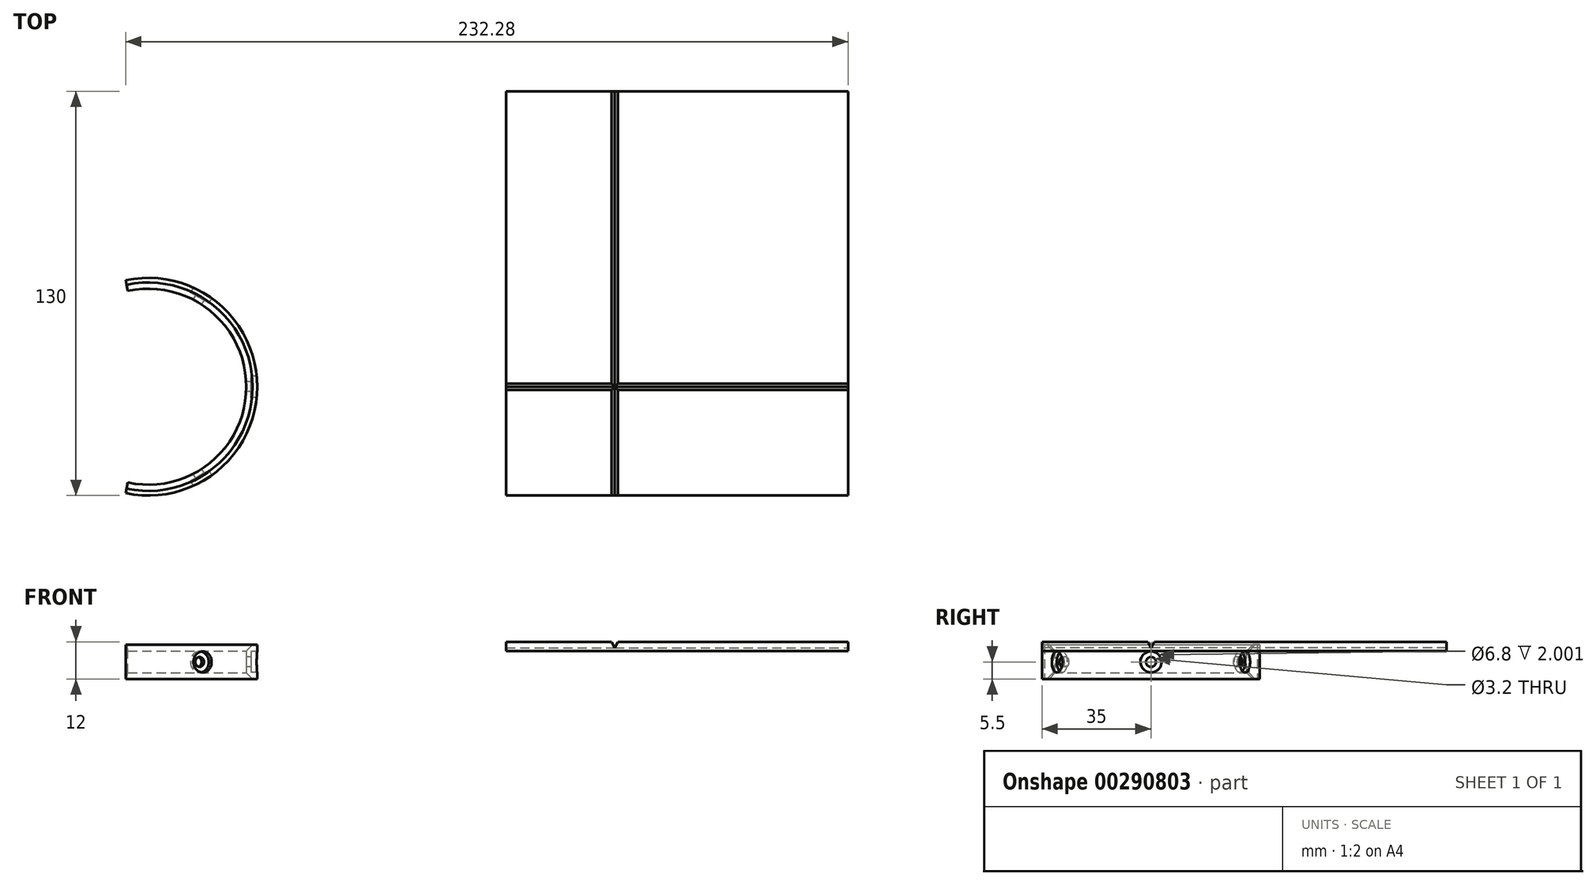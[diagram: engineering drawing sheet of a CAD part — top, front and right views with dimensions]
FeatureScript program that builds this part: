
annotation { "Feature Type Name" : "Feature", "Feature Type Description" : "" }
export const myFeature = defineFeature(function(context is Context, id is Id, definition is map)
    precondition{}
    {
        {
            var Q0;
            Q0=qCreatedBy(makeId("Top.planeOp"),FACE);
            var sketch = newSketch(context, id + "F0", { "sketchPlane" : qUnion([Q0])});
            skLineSegment(sketch, "E0.bottom", {"start": v(60, 80) * mm, "end": v(-20, 80) * mm});
            skLineSegment(sketch, "E0.top", {"start": v(60, -20) * mm, "end": v(-20, -20) * mm});
            skLineSegment(sketch, "E0.left", {"start": v(60, 80) * mm, "end": v(60, -20) * mm});
            skLineSegment(sketch, "E0.right", {"start": v(-20, 80) * mm, "end": v(-20, -20) * mm});
            skLineSegment(sketch, "E1.bottom", {"start": v(75, 95) * mm, "end": v(-35, 95) * mm});
            skLineSegment(sketch, "E1.top", {"start": v(75, -35) * mm, "end": v(-35, -35) * mm});
            skLineSegment(sketch, "E1.left", {"start": v(75, 95) * mm, "end": v(75, -35) * mm});
            skLineSegment(sketch, "E1.right", {"start": v(-35, 95) * mm, "end": v(-35, -35) * mm});
            skSolve(sketch);
        }
        {
            var Q0;
            {var subQ4=sQuery(id+"F0.wireOp",EDGE,"E0.bottom");Q0=makeQuery(id+"F0.imprint","IMPRINT",FACE,{"disambiguationData":[TD([[makeQuery(id+"F0.imprint","IMPRINT",EDGE,{"derivedFrom":subQ4}),-1.0]])]});}
            var Q1;
            Q1=makeQuery(id+"F0.imprint","IMPRINT",FACE,{"disambiguationData":[TD([[makeQuery(id+"F0.imprint","IMPRINT",EDGE,{"derivedFrom":sQuery(id+"F0.wireOp",EDGE,"2jODp8hE-4E36-BnlD-O6PP-fLfLwUdcZIw1")}),-1.0]])]});
            var Q2;
            Q2=makeQuery(id+"F0.imprint","IMPRINT",FACE,{"disambiguationData":[TD([[makeQuery(id+"F0.imprint","IMPRINT",EDGE,{"derivedFrom":sQuery(id+"F0.wireOp",EDGE,"CgjALgno-Vict-Y27T-c60f-twubqw5wff3r")}),-1.0]])]});
            var Q3;
            {var subQ4=sQuery(id+"F0.wireOp",EDGE,"E0.bottom");Q3=makeQuery(id+"F0.imprint","IMPRINT",FACE,{"disambiguationData":[TD([[makeQuery(id+"F0.imprint","IMPRINT",EDGE,{"derivedFrom":subQ4}),1.0]])]});}
            var Q4;
            Q4=makeQuery(id+"F0.imprint","IMPRINT",FACE,{"disambiguationData":[TD([[makeQuery(id+"F0.imprint","IMPRINT",EDGE,{"derivedFrom":sQuery(id+"F0.wireOp",EDGE,"DNGsPYIE-E45O-dohH-7LIo-O8bAVorIZV12")}),1.0]])]});
            var Q5;
            Q5=makeQuery(id+"F0.imprint","IMPRINT",FACE,{"disambiguationData":[TD([[makeQuery(id+"F0.imprint","IMPRINT",EDGE,{"derivedFrom":sQuery(id+"F0.wireOp",EDGE,"2jODp8hE-4E36-BnlD-O6PP-fLfLwUdcZIw1")}),1.0]])]});
            extrude(context, id + "F1", {"entities" : qUnion([Q0, Q1, Q2, Q3, Q4, Q5]), "depth" : 3 * mm});
        }
        {
            var Q0;
            Q0=makeQuery(id+"F1.opExtrude","SWEPT_FACE",FACE,{"disambiguationData":[OSD([sQuery(id+"F0.wireOp",EDGE,"E1.top")])]});
            var sketch = newSketch(context, id + "F2", { "sketchPlane" : qUnion([Q0])});
            skLineSegment(sketch, "E2", {"start": v(-1, 3) * mm, "end": v(0, 1) * mm});
            skLineSegment(sketch, "E3", {"start": v(0, 1) * mm, "end": v(1, 3) * mm});
            skLineSegment(sketch, "E4", {"start": v(1, 3) * mm, "end": v(-1, 3) * mm});
            skSolve(sketch);
        }
        {
            var Q0;
            Q0=qSketchRegion(id+"F2",true);
            extrude(context, id + "F3", {"entities" : qUnion([Q0]), "operationType" : NewBodyOperationType.REMOVE, "oppositeDirection" : true, "depth" : 140 * mm});
        }
        {
            var Q0;
            Q0=makeQuery(id+"F1.opExtrude","SWEPT_FACE",FACE,{"disambiguationData":[OSD([sQuery(id+"F0.wireOp",EDGE,"E1.left")])]});
            var sketch = newSketch(context, id + "F4", { "sketchPlane" : qUnion([Q0])});
            skLineSegment(sketch, "E5", {"start": v(-1, 3) * mm, "end": v(0, 1) * mm});
            skLineSegment(sketch, "E6", {"start": v(0, 1) * mm, "end": v(1, 3) * mm});
            skLineSegment(sketch, "E7", {"start": v(1, 3) * mm, "end": v(-1, 3) * mm});
            skSolve(sketch);
        }
        {
            var Q0;
            Q0=makeQuery(id+"F4.imprint","IMPRINT",FACE,{"disambiguationData":[TD([[makeQuery(id+"F4.imprint","IMPRINT",EDGE,{"derivedFrom":sQuery(id+"F4.wireOp",EDGE,"E5")}),1.0]])]});
            extrude(context, id + "F5", {"entities" : qUnion([Q0]), "operationType" : NewBodyOperationType.REMOVE, "oppositeDirection" : true, "depth" : 120 * mm});
        }
        {
            var Q0;
            Q0=qCreatedBy(makeId("Top.planeOp"),FACE);
            cPlane(context, id + "F6", {"entities" : qUnion([Q0]), "cplaneType" : CPlaneType.OFFSET, "offset" : 3.5 * mm, "oppositeDirection" : true, "width" : 150 * mm, "height" : 150 * mm});
        }
        {
            var Q0;
            Q0=qCreatedBy(id+"F6.planeOp",FACE);
            var sketch = newSketch(context, id + "F7", { "sketchPlane" : qUnion([Q0])});
            skPoint(sketch, "E8.0", {"position": v(0, 0) * mm});
            skLineSegment(sketch, "E9", {"start": v(0, 0) * mm, "end": v(-150, 0) * mm, "construction": true});
            skCircle(sketch, "E10", {"center": v(-150, 0) * mm, "radius": 31.5 * mm});
            skCircle(sketch, "E11", {"center": v(-150, 0) * mm, "radius": 35 * mm});
            skSolve(sketch);
        }
        {
            var Q0;
            Q0=makeQuery(id+"F7.imprint","IMPRINT",FACE,{"disambiguationData":[TD([[makeQuery(id+"F7.imprint","IMPRINT",EDGE,{"derivedFrom":sQuery(id+"F7.wireOp",EDGE,"E10")}),-1.0]])]});
            extrude(context, id + "F8", {"entities" : qUnion([Q0]), "endBound" : BoundingType.SYMMETRIC, "depth" : 11 * mm});
        }
        {
            var Q0;
            Q0=qCreatedBy(id+"F6.planeOp",FACE);
            var sketch = newSketch(context, id + "F9", { "sketchPlane" : qUnion([Q0])});
            skPoint(sketch, "E12.0", {"position": v(-150, 0) * mm});
            skLineSegment(sketch, "E13", {"start": v(-150, 0) * mm, "end": v(-24.24, 0) * mm, "construction": true});
            skLineSegment(sketch, "E14.bottom", {"start": v(-117, 0) * mm, "end": v(-117, -1.6) * mm});
            skLineSegment(sketch, "E14.top", {"start": v(-119.72, 0) * mm, "end": v(-119.72, -1.6) * mm});
            skLineSegment(sketch, "E14.left", {"start": v(-117, 0) * mm, "end": v(-119.72, 0) * mm});
            skLineSegment(sketch, "E14.right", {"start": v(-117, -1.6) * mm, "end": v(-119.72, -1.6) * mm});
            skLineSegment(sketch, "E15.bottom", {"start": v(-117, 0) * mm, "end": v(-117, -3.4) * mm});
            skLineSegment(sketch, "E15.top", {"start": v(-114.1, 0) * mm, "end": v(-114.1, -3.4) * mm});
            skLineSegment(sketch, "E15.left", {"start": v(-117, 0) * mm, "end": v(-114.1, 0) * mm});
            skLineSegment(sketch, "E15.right", {"start": v(-117, -3.4) * mm, "end": v(-114.1, -3.4) * mm});
            skLineSegment(sketch, "E16", {"start": v(-150, 0) * mm, "end": v(-87.12, -108.91) * mm, "construction": true});
            skLineSegment(sketch, "E17.bottom", {"start": v(-133.5, -28.58) * mm, "end": v(-134.89, -29.38) * mm});
            skLineSegment(sketch, "E17.top", {"start": v(-134.86, -26.22) * mm, "end": v(-136.24, -27.02) * mm});
            skLineSegment(sketch, "E17.left", {"start": v(-133.5, -28.58) * mm, "end": v(-134.86, -26.22) * mm});
            skLineSegment(sketch, "E17.right", {"start": v(-134.89, -29.38) * mm, "end": v(-136.24, -27.02) * mm});
            skLineSegment(sketch, "E18.bottom", {"start": v(-133.5, -28.58) * mm, "end": v(-136.44, -30.28) * mm});
            skLineSegment(sketch, "E18.top", {"start": v(-132.05, -31.08) * mm, "end": v(-135, -32.78) * mm});
            skLineSegment(sketch, "E18.left", {"start": v(-133.5, -28.58) * mm, "end": v(-132.05, -31.08) * mm});
            skLineSegment(sketch, "E18.right", {"start": v(-136.44, -30.28) * mm, "end": v(-135, -32.78) * mm});
            skLineSegment(sketch, "E19", {"start": v(-150, 0) * mm, "end": v(-87.12, 108.91) * mm, "construction": true});
            skLineSegment(sketch, "E20.bottom", {"start": v(-133.5, 28.58) * mm, "end": v(-132.11, 27.78) * mm});
            skLineSegment(sketch, "E20.top", {"start": v(-134.86, 26.22) * mm, "end": v(-133.47, 25.42) * mm});
            skLineSegment(sketch, "E20.left", {"start": v(-133.5, 28.58) * mm, "end": v(-134.86, 26.22) * mm});
            skLineSegment(sketch, "E20.right", {"start": v(-132.11, 27.78) * mm, "end": v(-133.47, 25.42) * mm});
            skLineSegment(sketch, "E21.bottom", {"start": v(-133.5, 28.58) * mm, "end": v(-130.56, 26.88) * mm});
            skLineSegment(sketch, "E21.top", {"start": v(-132.05, 31.08) * mm, "end": v(-129.1, 29.38) * mm});
            skLineSegment(sketch, "E21.left", {"start": v(-133.5, 28.58) * mm, "end": v(-132.05, 31.08) * mm});
            skLineSegment(sketch, "E21.right", {"start": v(-130.56, 26.88) * mm, "end": v(-129.1, 29.38) * mm});
            skLineSegment(sketch, "E22", {"start": v(-150, 0) * mm, "end": v(-212.88, -108.91) * mm, "construction": true});
            skLineSegment(sketch, "E23.bottom", {"start": v(-166.5, -28.58) * mm, "end": v(-167.89, -27.78) * mm});
            skLineSegment(sketch, "E23.top", {"start": v(-165.14, -26.22) * mm, "end": v(-166.53, -25.42) * mm});
            skLineSegment(sketch, "E23.left", {"start": v(-166.5, -28.58) * mm, "end": v(-165.14, -26.22) * mm});
            skLineSegment(sketch, "E23.right", {"start": v(-167.89, -27.78) * mm, "end": v(-166.53, -25.42) * mm});
            skLineSegment(sketch, "E24.bottom", {"start": v(-166.5, -28.58) * mm, "end": v(-169.44, -26.88) * mm});
            skLineSegment(sketch, "E24.top", {"start": v(-167.95, -31.08) * mm, "end": v(-170.9, -29.38) * mm});
            skLineSegment(sketch, "E24.left", {"start": v(-166.5, -28.58) * mm, "end": v(-167.95, -31.08) * mm});
            skLineSegment(sketch, "E24.right", {"start": v(-169.44, -26.88) * mm, "end": v(-170.9, -29.38) * mm});
            skPoint(sketch, "E25.0", {"position": v(0, 0) * mm});
            skSolve(sketch);
        }
        {
            var Q0;
            Q0=makeQuery(id+"F9.imprint","IMPRINT",FACE,{"disambiguationData":[TD([[makeQuery(id+"F9.imprint","IMPRINT",EDGE,{"derivedFrom":sQuery(id+"F9.wireOp",EDGE,"E18.top")}),-1.0]])]});
            var Q1;
            Q1=makeQuery(id+"F9.imprint","IMPRINT",FACE,{"disambiguationData":[TD([[makeQuery(id+"F9.imprint","IMPRINT",EDGE,{"derivedFrom":sQuery(id+"F9.wireOp",EDGE,"E17.top")}),1.0]])]});
            var Q2;
            Q2=sQuery(id+"F9.wireOp",EDGE,"E16");
            revolve(context, id + "F10", {"operationType" : NewBodyOperationType.REMOVE, "entities" : qUnion([Q0, Q1]), "axis" : qUnion([Q2]), "revolveType" : RevolveType.FULL, "oppositeDirection" : true});
        }
        {
            var Q0;
            Q0=makeQuery(id+"F9.imprint","IMPRINT",FACE,{"disambiguationData":[TD([[makeQuery(id+"F9.imprint","IMPRINT",EDGE,{"derivedFrom":sQuery(id+"F9.wireOp",EDGE,"E15.top")}),-1.0]])]});
            var Q1;
            Q1=makeQuery(id+"F9.imprint","IMPRINT",FACE,{"disambiguationData":[TD([[makeQuery(id+"F9.imprint","IMPRINT",EDGE,{"derivedFrom":sQuery(id+"F9.wireOp",EDGE,"E14.top")}),1.0]])]});
            var Q2;
            Q2=sQuery(id+"F9.wireOp",EDGE,"E13");
            revolve(context, id + "F11", {"operationType" : NewBodyOperationType.REMOVE, "entities" : qUnion([Q0, Q1]), "axis" : qUnion([Q2]), "revolveType" : RevolveType.FULL});
        }
        {
            var Q0;
            Q0=makeQuery(id+"F9.imprint","IMPRINT",FACE,{"disambiguationData":[TD([[makeQuery(id+"F9.imprint","IMPRINT",EDGE,{"derivedFrom":sQuery(id+"F9.wireOp",EDGE,"E21.top")}),-1.0]])]});
            var Q1;
            Q1=makeQuery(id+"F9.imprint","IMPRINT",FACE,{"disambiguationData":[TD([[makeQuery(id+"F9.imprint","IMPRINT",EDGE,{"derivedFrom":sQuery(id+"F9.wireOp",EDGE,"E20.top")}),1.0]])]});
            var Q2;
            Q2=sQuery(id+"F9.wireOp",EDGE,"E19");
            revolve(context, id + "F12", {"operationType" : NewBodyOperationType.REMOVE, "entities" : qUnion([Q0, Q1]), "axis" : qUnion([Q2]), "revolveType" : RevolveType.FULL});
        }
        {
            var Q0;
            Q0=makeQuery(id+"F9.imprint","IMPRINT",FACE,{"disambiguationData":[TD([[makeQuery(id+"F9.imprint","IMPRINT",EDGE,{"derivedFrom":sQuery(id+"F9.wireOp",EDGE,"E24.top")}),-1.0]])]});
            var Q1;
            Q1=makeQuery(id+"F9.imprint","IMPRINT",FACE,{"disambiguationData":[TD([[makeQuery(id+"F9.imprint","IMPRINT",EDGE,{"derivedFrom":sQuery(id+"F9.wireOp",EDGE,"E23.top")}),1.0]])]});
            var Q2;
            Q2=sQuery(id+"F9.wireOp",EDGE,"E22");
            revolve(context, id + "F13", {"operationType" : NewBodyOperationType.REMOVE, "entities" : qUnion([Q0, Q1]), "axis" : qUnion([Q2]), "revolveType" : RevolveType.FULL});
        }
        {
            var Q0;
            Q0=qCreatedBy(makeId("Front.planeOp"),FACE);
            var sketch = newSketch(context, id + "F14", { "sketchPlane" : qUnion([Q0])});
            skPoint(sketch, "E26.0", {"position": v(-150, -3.5) * mm});
            skLineSegment(sketch, "E27.left", {"start": v(-185, -7) * mm, "end": v(-185, 0) * mm});
            skLineSegment(sketch, "E27.right", {"start": v(-181.5, -7) * mm, "end": v(-181.5, 0) * mm});
            skLineSegment(sketch, "E28", {"start": v(-150, -26.04) * mm, "end": v(-150, 19.04) * mm, "construction": true});
            skLineSegment(sketch, "E29.0", {"start": v(-185, 2) * mm, "end": v(-150, 2) * mm});
            skLineSegment(sketch, "E30.0.0", {"start": v(-150, -9) * mm, "end": v(-185, -9) * mm});
            skLineSegment(sketch, "E31", {"start": v(-181.5, 2) * mm, "end": v(-181.5, 0) * mm});
            skLineSegment(sketch, "E32", {"start": v(-181.5, -7) * mm, "end": v(-181.5, -9) * mm});
            skLineSegment(sketch, "E33", {"start": v(-185, 2) * mm, "end": v(-185, 0) * mm});
            skLineSegment(sketch, "E34", {"start": v(-185, -7) * mm, "end": v(-185, -9) * mm});
            skLineSegment(sketch, "E35", {"start": v(-185, 2) * mm, "end": v(-183.5, 2) * mm});
            skLineSegment(sketch, "E36", {"start": v(-183.5, 2) * mm, "end": v(-181.5, 0) * mm});
            skLineSegment(sketch, "E37", {"start": v(-185, -9) * mm, "end": v(-183.5, -9) * mm});
            skLineSegment(sketch, "E38", {"start": v(-183.5, -9) * mm, "end": v(-181.5, -7) * mm});
            skSolve(sketch);
        }
        {
            var Q0;
            Q0=makeQuery(id+"F14.imprint","IMPRINT",FACE,{"disambiguationData":[TD([[makeQuery(id+"F14.imprint","IMPRINT",EDGE,{"derivedFrom":sQuery(id+"F14.wireOp",EDGE,"E27.left")}),-1.0]])]});
            var Q1;
            Q1=sQuery(id+"F14.wireOp",EDGE,"E28");
            revolve(context, id + "F15", {"operationType" : NewBodyOperationType.REMOVE, "entities" : qUnion([Q0]), "axis" : qUnion([Q1]), "revolveType" : RevolveType.SYMMETRIC, "angle" : 156 * degree});
        }
        {
            var Q0;
            {var subQ2=sQuery(id+"F14.wireOp",EDGE,"E31");Q0=makeQuery(id+"F14.imprint","IMPRINT",FACE,{"disambiguationData":[TD([[makeQuery(id+"F14.imprint","IMPRINT",EDGE,{"derivedFrom":subQ2}),-1.0]])]});}
            var Q1;
            {var subQ2=sQuery(id+"F14.wireOp",EDGE,"E32");Q1=makeQuery(id+"F14.imprint","IMPRINT",FACE,{"disambiguationData":[TD([[makeQuery(id+"F14.imprint","IMPRINT",EDGE,{"derivedFrom":subQ2}),-1.0]])]});}
            var Q2;
            Q2=sQuery(id+"F14.wireOp",EDGE,"E28");
            revolve(context, id + "F16", {"operationType" : NewBodyOperationType.REMOVE, "entities" : qUnion([Q0, Q1]), "axis" : qUnion([Q2]), "revolveType" : RevolveType.FULL, "oppositeDirection" : true});
        }
    });
